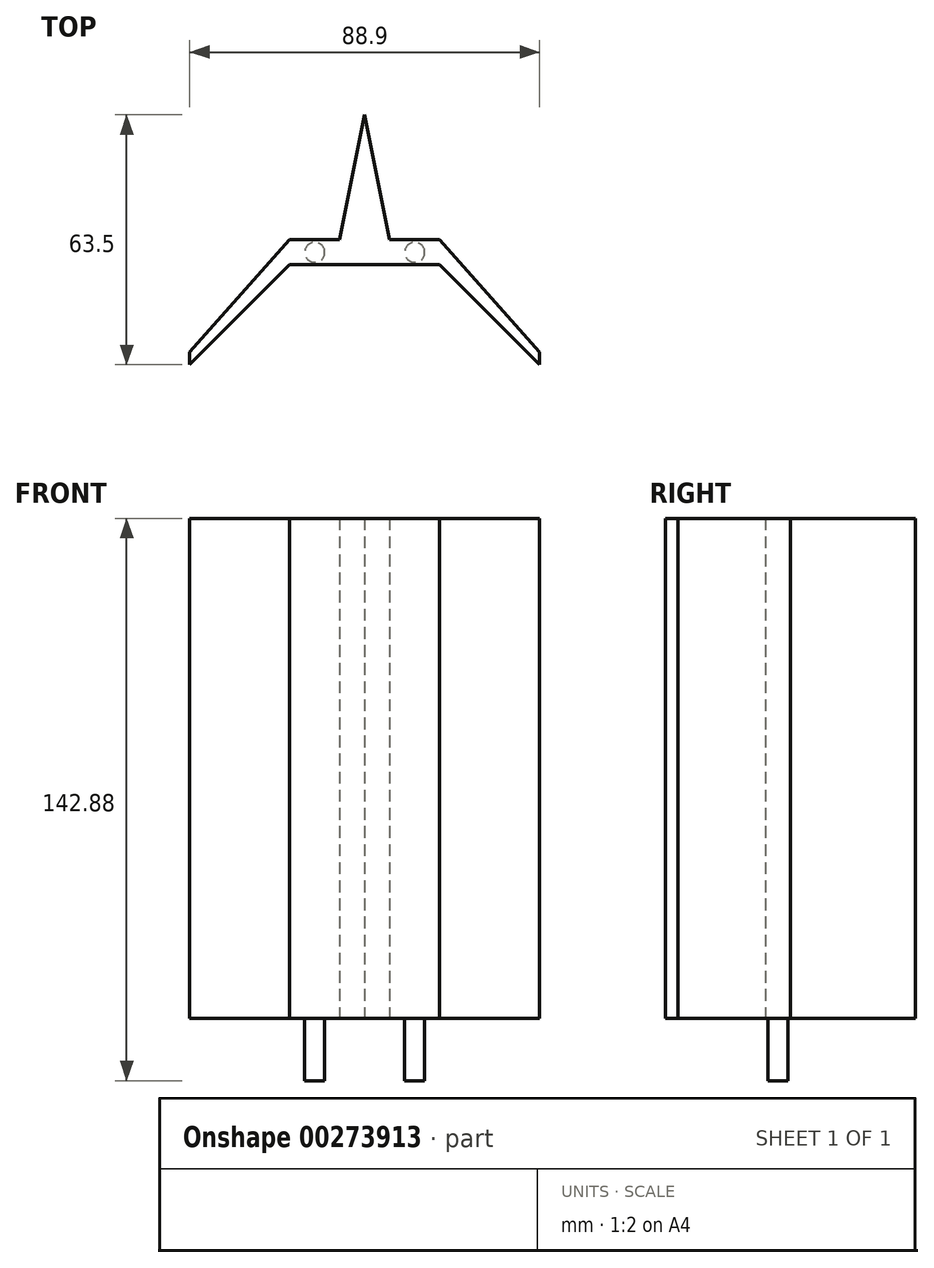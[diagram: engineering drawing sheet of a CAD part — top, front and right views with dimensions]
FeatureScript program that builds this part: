
annotation { "Feature Type Name" : "Feature", "Feature Type Description" : "" }
export const myFeature = defineFeature(function(context is Context, id is Id, definition is map)
    precondition{}
    {
        {
            var Q0;
            Q0=qCreatedBy(makeId("Top.planeOp"),FACE);
            var sketch = newSketch(context, id + "F0", { "sketchPlane" : qUnion([Q0])});
            skLineSegment(sketch, "E0", {"start": v(0, 0) * mm, "end": v(19.05, 0) * mm});
            skLineSegment(sketch, "E1", {"start": v(19.05, 0) * mm, "end": v(44.45, -25.4) * mm});
            skLineSegment(sketch, "E2", {"start": v(44.45, -25.4) * mm, "end": v(44.45, -22.22) * mm});
            skLineSegment(sketch, "E3", {"start": v(44.45, -22.22) * mm, "end": v(19.05, 6.35) * mm});
            skLineSegment(sketch, "E4", {"start": v(19.05, 6.35) * mm, "end": v(6.35, 6.35) * mm});
            skLineSegment(sketch, "E5", {"start": v(6.35, 6.35) * mm, "end": v(0, 38.1) * mm});
            skLineSegment(sketch, "E6", {"start": v(0, 0) * mm, "end": v(0, 38.1) * mm, "construction": true});
            skLineSegment(sketch, "E7.MirrorCS", {"start": v(-44.45, -25.4) * mm, "end": v(-44.45, -22.23) * mm});
            skLineSegment(sketch, "E8.MirrorCS", {"start": v(0, 0) * mm, "end": v(-19.05, 0) * mm});
            skLineSegment(sketch, "E9.MirrorCS", {"start": v(-6.35, 6.35) * mm, "end": v(0, 38.1) * mm});
            skLineSegment(sketch, "E10.MirrorCS", {"start": v(-19.05, 0) * mm, "end": v(-44.45, -25.4) * mm});
            skLineSegment(sketch, "E11.MirrorCS", {"start": v(-19.05, 6.35) * mm, "end": v(-6.35, 6.35) * mm});
            skLineSegment(sketch, "E12.MirrorCS", {"start": v(-44.45, -22.23) * mm, "end": v(-19.05, 6.35) * mm});
            skLineSegment(sketch, "E13", {"start": v(12.7, 6.35) * mm, "end": v(12.7, 0) * mm, "construction": true});
            skLineSegment(sketch, "E14.MirrorCS", {"start": v(-12.7, 6.35) * mm, "end": v(-12.7, 0) * mm, "construction": true});
            skCircle(sketch, "E15", {"center": v(-12.7, 3.17) * mm, "radius": 2.54 * mm});
            skCircle(sketch, "E16", {"center": v(12.7, 3.18) * mm, "radius": 2.54 * mm});
            skSolve(sketch);
        }
        {
            var Q0;
            Q0=makeQuery(id+"F0.imprint","IMPRINT",FACE,{"disambiguationData":[TD([[makeQuery(id+"F0.imprint","IMPRINT",EDGE,{"derivedFrom":sQuery(id+"F0.wireOp",EDGE,"E0")}),1.0]])]});
            var Q1;
            Q1=makeQuery(id+"F0.imprint","IMPRINT",FACE,{"disambiguationData":[TD([[makeQuery(id+"F0.imprint","IMPRINT",EDGE,{"derivedFrom":sQuery(id+"F0.wireOp",EDGE,"E15")}),1.0]])]});
            var Q2;
            Q2=makeQuery(id+"F0.imprint","IMPRINT",FACE,{"disambiguationData":[TD([[makeQuery(id+"F0.imprint","IMPRINT",EDGE,{"derivedFrom":sQuery(id+"F0.wireOp",EDGE,"E16")}),1.0]])]});
            extrude(context, id + "F1", {"entities" : qUnion([Q0, Q1, Q2]), "depth" : 127 * mm});
        }
        {
            var Q0;
            Q0=makeQuery(id+"F0.imprint","IMPRINT",FACE,{"disambiguationData":[TD([[makeQuery(id+"F0.imprint","IMPRINT",EDGE,{"derivedFrom":sQuery(id+"F0.wireOp",EDGE,"E15")}),1.0]])]});
            var Q1;
            Q1=makeQuery(id+"F0.imprint","IMPRINT",FACE,{"disambiguationData":[TD([[makeQuery(id+"F0.imprint","IMPRINT",EDGE,{"derivedFrom":sQuery(id+"F0.wireOp",EDGE,"E16")}),1.0]])]});
            extrude(context, id + "F2", {"entities" : qUnion([Q0, Q1]), "operationType" : NewBodyOperationType.ADD, "oppositeDirection" : true, "depth" : 15.88 * mm});
        }
    });
